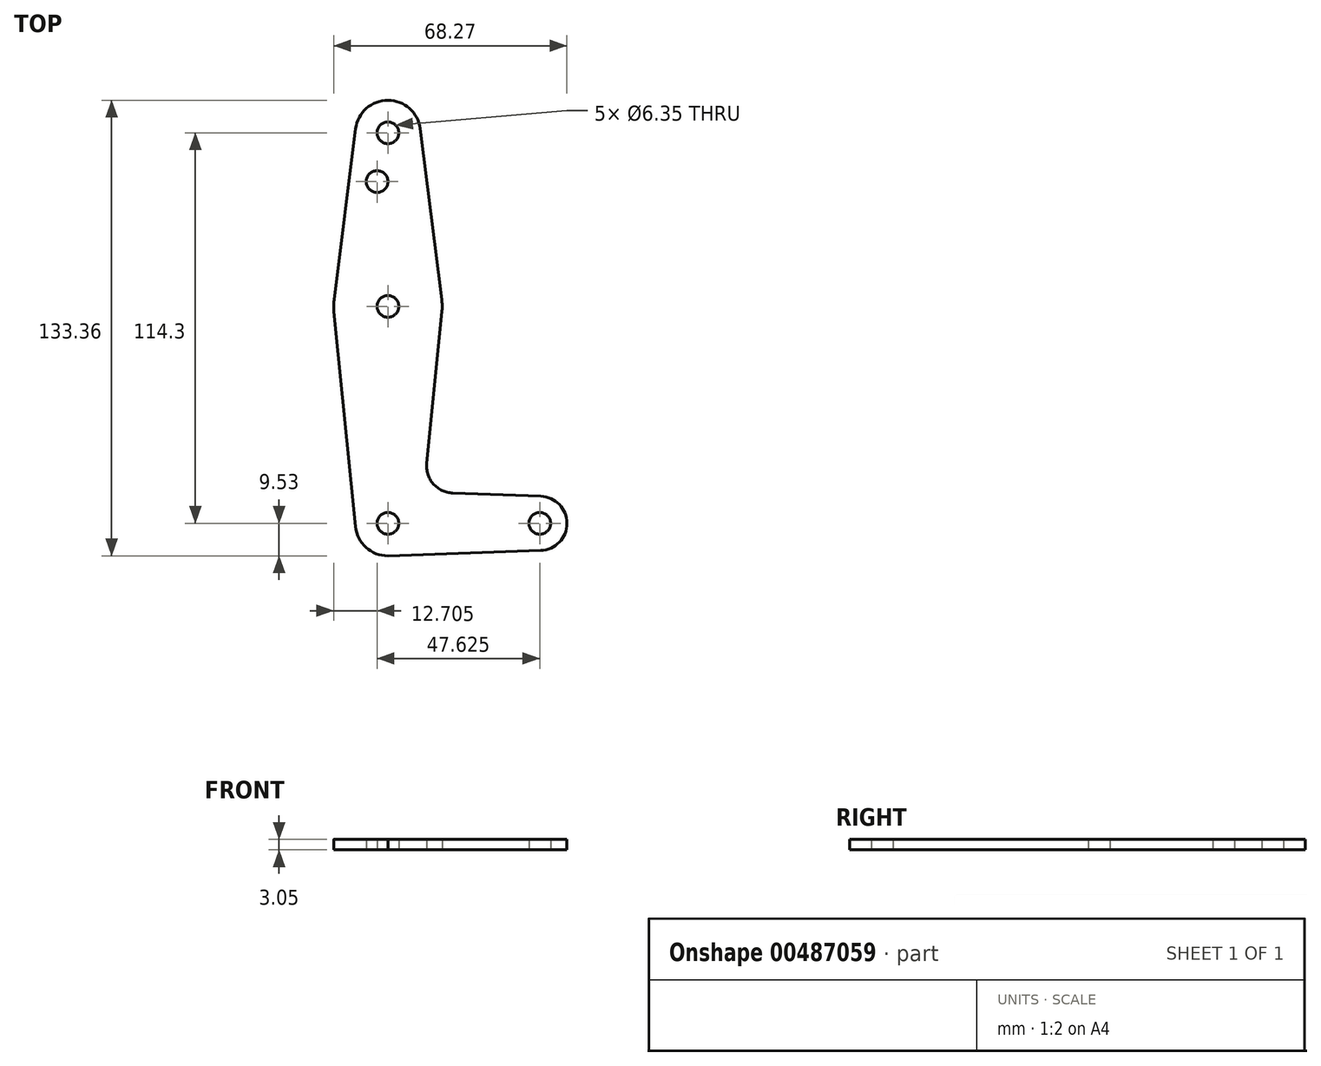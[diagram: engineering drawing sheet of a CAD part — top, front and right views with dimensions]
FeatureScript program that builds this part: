
annotation { "Feature Type Name" : "Feature", "Feature Type Description" : "" }
export const myFeature = defineFeature(function(context is Context, id is Id, definition is map)
    precondition{}
    {
        {
            var Q0;
            Q0=qCreatedBy(makeId("Top.planeOp"),FACE);
            var sketch = newSketch(context, id + "F0", { "sketchPlane" : qUnion([Q0])});
            skLineSegment(sketch, "E0", {"start": v(0, 0) * mm, "end": v(0, 114.3) * mm, "construction": true});
            skLineSegment(sketch, "E1", {"start": v(0, 0) * mm, "end": v(44.45, 0) * mm, "construction": true});
            skCircle(sketch, "E2", {"center": v(0, 0) * mm, "radius": 9.53 * mm});
            skCircle(sketch, "E3", {"center": v(0, 114.3) * mm, "radius": 9.53 * mm});
            skCircle(sketch, "E4", {"center": v(44.45, 0) * mm, "radius": 7.94 * mm});
            skCircle(sketch, "E5", {"center": v(0, 63.5) * mm, "radius": 15.88 * mm});
            skLineSegment(sketch, "E6", {"start": v(9.45, 115.5) * mm, "end": v(15.75, 65.48) * mm});
            skLineSegment(sketch, "E7", {"start": v(-9.45, 115.5) * mm, "end": v(-15.75, 65.48) * mm});
            skLineSegment(sketch, "E8", {"start": v(18.97, 8.85) * mm, "end": v(44.73, 7.93) * mm});
            skLineSegment(sketch, "E9", {"start": v(0, -9.53) * mm, "end": v(44.73, -7.93) * mm});
            skLineSegment(sketch, "E10", {"start": v(15.8, 61.91) * mm, "end": v(11.34, 17.59) * mm});
            skLineSegment(sketch, "E11", {"start": v(-15.8, 61.91) * mm, "end": v(-9.48, -0.95) * mm});
            skCircle(sketch, "E12", {"center": v(0, 114.3) * mm, "radius": 3.18 * mm});
            skCircle(sketch, "E13", {"center": v(0, 63.5) * mm, "radius": 3.18 * mm});
            skCircle(sketch, "E14", {"center": v(0, 0) * mm, "radius": 3.18 * mm});
            skCircle(sketch, "E15", {"center": v(44.45, 0) * mm, "radius": 3.18 * mm});
            skCircle(sketch, "E16", {"center": v(-3.17, 100.03) * mm, "radius": 3.18 * mm});
            skArc(sketch, "E17.filletArc", {"start": v(11.34, 17.59) * mm, "mid": v(13.26, 11.57) * mm, "end": v(18.97, 8.85) * mm});
            skSolve(sketch);
        }
        {
            var Q0;
            Q0=makeQuery(id+"F0.imprint","IMPRINT",FACE,{"disambiguationData":[TD([[makeQuery(id+"F0.imprint","IMPRINT",EDGE,{"derivedFrom":sQuery(id+"F0.wireOp",EDGE,"E12")}),-1.0]])]});
            var Q1;
            {var subQ0=sQuery(id+"F0.wireOp",EDGE,"E6");Q1=makeQuery(id+"F0.imprint","IMPRINT",FACE,{"disambiguationData":[TD([[makeQuery(id+"F0.imprint","IMPRINT",EDGE,{"derivedFrom":subQ0}),-1.0]])]});}
            var Q2;
            Q2=makeQuery(id+"F0.imprint","IMPRINT",FACE,{"disambiguationData":[TD([[makeQuery(id+"F0.imprint","IMPRINT",EDGE,{"derivedFrom":sQuery(id+"F0.wireOp",EDGE,"E13")}),-1.0]])]});
            var Q3;
            {var subQ0=sQuery(id+"F0.wireOp",EDGE,"E8");Q3=makeQuery(id+"F0.imprint","IMPRINT",FACE,{"disambiguationData":[TD([[makeQuery(id+"F0.imprint","IMPRINT",EDGE,{"derivedFrom":subQ0}),-1.0]])]});}
            var Q4;
            Q4=makeQuery(id+"F0.imprint","IMPRINT",FACE,{"disambiguationData":[TD([[makeQuery(id+"F0.imprint","IMPRINT",EDGE,{"derivedFrom":sQuery(id+"F0.wireOp",EDGE,"E14")}),-1.0]])]});
            var Q5;
            Q5=makeQuery(id+"F0.imprint","IMPRINT",FACE,{"disambiguationData":[TD([[makeQuery(id+"F0.imprint","IMPRINT",EDGE,{"derivedFrom":sQuery(id+"F0.wireOp",EDGE,"E15")}),-1.0]])]});
            extrude(context, id + "F1", {"entities" : qUnion([Q0, Q1, Q2, Q3, Q4, Q5]), "depth" : 3.05 * mm});
        }
    });
